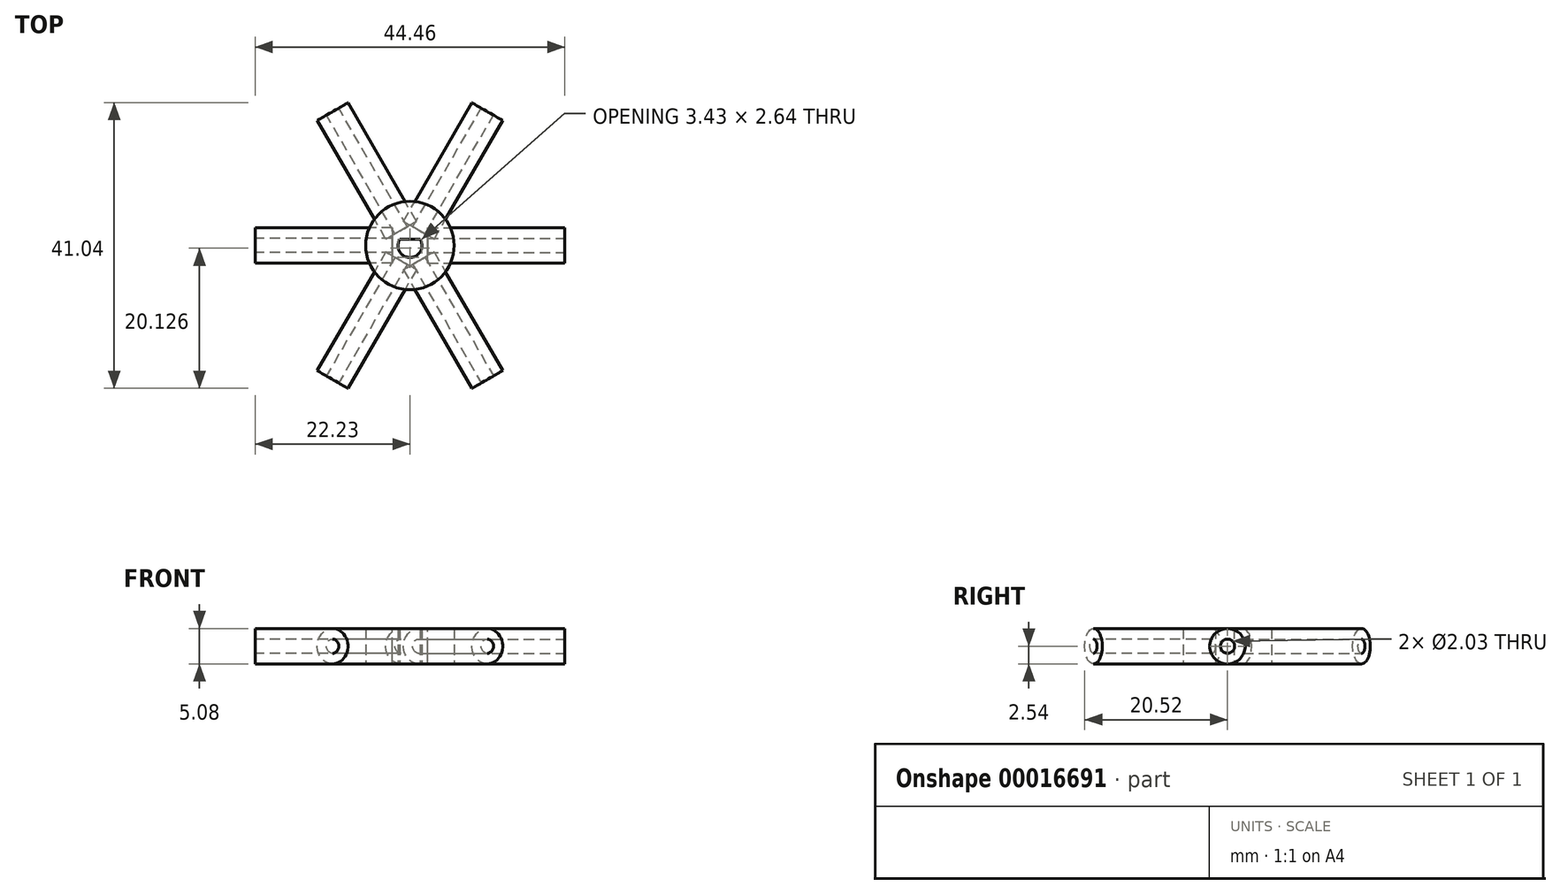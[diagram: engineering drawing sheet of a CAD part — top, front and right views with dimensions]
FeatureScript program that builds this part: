
annotation { "Feature Type Name" : "Feature", "Feature Type Description" : "" }
export const myFeature = defineFeature(function(context is Context, id is Id, definition is map)
    precondition{}
    {
        {
            var Q0;
            Q0=qCreatedBy(makeId("Top.planeOp"),FACE);
            var sketch = newSketch(context, id + "F0", { "sketchPlane" : qUnion([Q0])});
            skCircle(sketch, "E0", {"center": v(0, 0) * mm, "radius": 22.23 * mm, "construction": true});
            skArc(sketch, "E1", {"start": v(-1.44, 0.93) * mm, "mid": v(0, -1.71) * mm, "end": v(1.44, 0.93) * mm});
            skLineSegment(sketch, "E2", {"start": v(-1.44, 0.93) * mm, "end": v(1.44, 0.93) * mm});
            skCircle(sketch, "E3", {"center": v(0, 0) * mm, "radius": 6.35 * mm});
            skSolve(sketch);
        }
        {
            var Q0;
            Q0=makeQuery(id+"F0.imprint","IMPRINT",FACE,{"disambiguationData":[TD([[makeQuery(id+"F0.imprint","IMPRINT",EDGE,{"derivedFrom":sQuery(id+"F0.wireOp",EDGE,"E1")}),-1.0]])]});
            extrude(context, id + "F1", {"entities" : qUnion([Q0]), "depth" : 5.08 * mm});
        }
        {
            var Q0;
            Q0=qCreatedBy(makeId("Right.planeOp"),FACE);
            cPlane(context, id + "F2", {"entities" : qUnion([Q0]), "cplaneType" : CPlaneType.OFFSET, "offset" : 22.22 * mm, "width" : 152.4 * mm, "height" : 152.4 * mm});
        }
        {
            var Q0;
            Q0=qCreatedBy(id+"F2.planeOp",FACE);
            var sketch = newSketch(context, id + "F3", { "sketchPlane" : qUnion([Q0])});
            skLineSegment(sketch, "E4.0", {"start": v(-6.35, 5.08) * mm, "end": v(6.35, 5.08) * mm, "construction": true});
            skLineSegment(sketch, "E5", {"start": v(0, 0) * mm, "end": v(0, 5.08) * mm, "construction": true});
            skCircle(sketch, "E6", {"center": v(0, 2.54) * mm, "radius": 2.54 * mm});
            skCircle(sketch, "E7", {"center": v(0, 2.54) * mm, "radius": 1.02 * mm});
            skSolve(sketch);
        }
        {
            var Q0;
            Q0=makeQuery(id+"F3.imprint","IMPRINT",FACE,{"disambiguationData":[TD([[makeQuery(id+"F3.imprint","IMPRINT",EDGE,{"derivedFrom":sQuery(id+"F3.wireOp",EDGE,"E6")}),1.0]])]});
            extrude(context, id + "F4", {"entities" : qUnion([Q0]), "oppositeDirection" : true, "depth" : 19.68 * mm});
        }
        {
            var Q0;
            Q0=makeQuery(id+"F4.opExtrude","SWEPT_BODY",BODY,{"disambiguationData":[OSD([sQuery(id+"F3.wireOp",EDGE,"E6"),sQuery(id+"F3.wireOp",EDGE,"E7")])]});
            var Q1;
            Q1=makeQuery(id+"F1.opExtrude","CAP_EDGE",EDGE,{"disambiguationData":[OSD([sQuery(id+"F0.wireOp",EDGE,"E3")])],"isStart":false});
            circularPattern(context, id + "F5", {"entities" : qUnion([Q0]), "axis" : qUnion([Q1]), "angle" : 60 * degree, "instanceCount" : round(6)});
        }
    });
